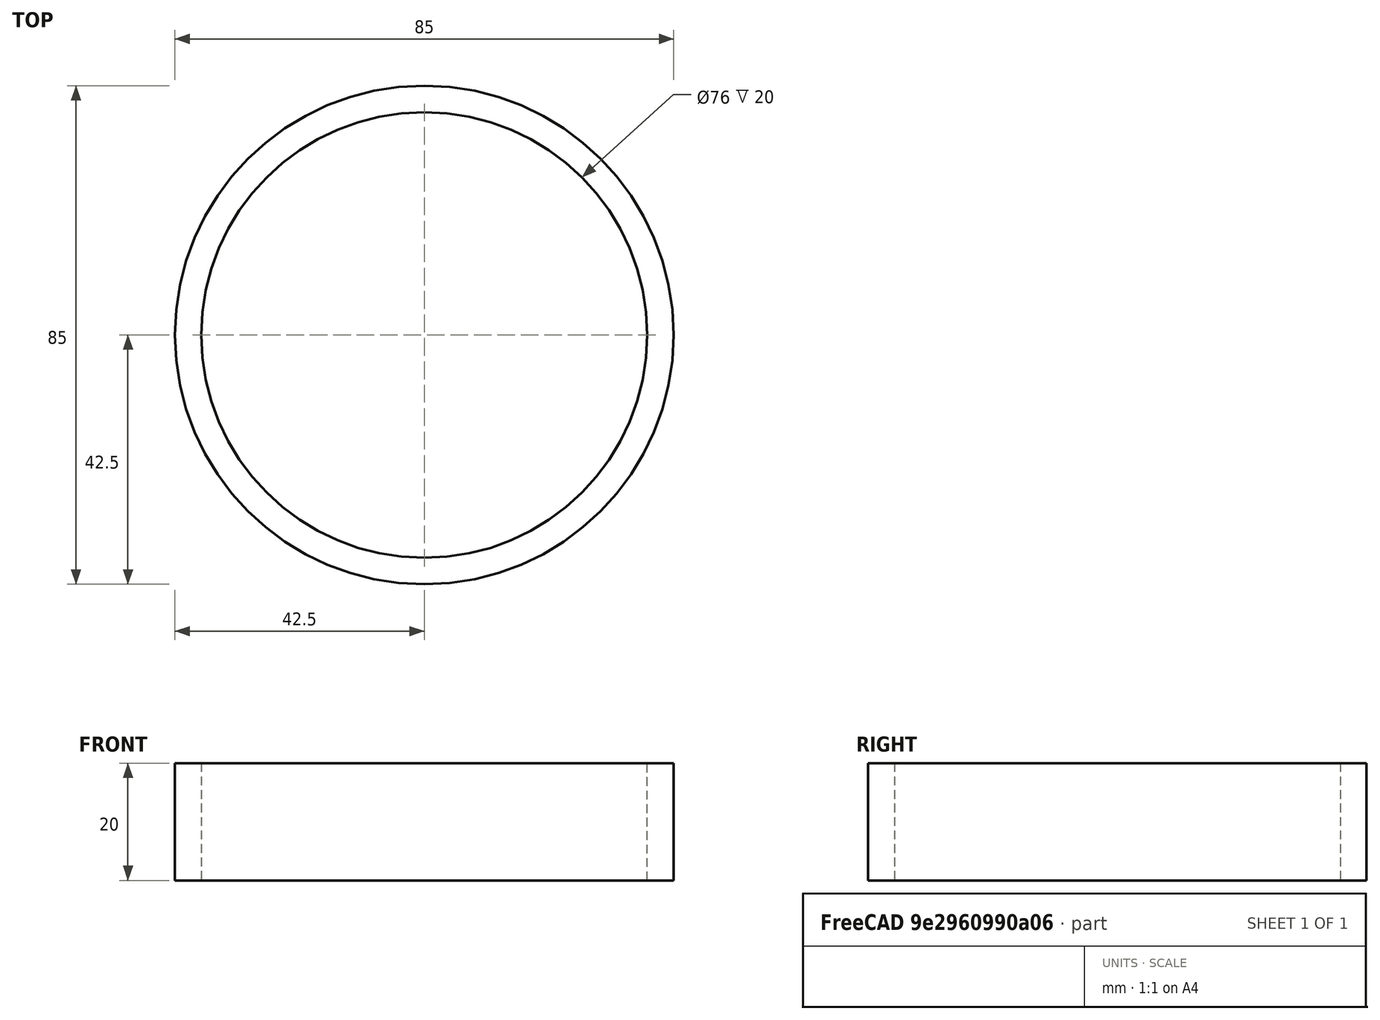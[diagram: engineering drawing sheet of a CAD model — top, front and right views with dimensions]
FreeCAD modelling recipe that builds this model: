
FCSTD DOCUMENT  (FreeCAD 0.19R24276 (Git))
Label: Ring_in_coil
License: All rights reserved
LicenseURL: http://en.wikipedia.org/wiki/All_rights_reserved
objects: Sketcher::SketchObject×1, PartDesign::Pad×1, PartDesign::Body×1
note: 4 computed .brp shape members not serialized (recipe doc carries the construction recipe); baked Part::Feature solids carry a one-line shape summary decoded from their .brp

FEATURE [Sketcher::SketchObject] Sketch
  FullyConstrained = true
  MapMode = 5
  Support = -> [XY_Plane]
  sketch-geometry (2):
    g0: Circle CenterX=0 CenterY=0 CenterZ=0 NormalX=0 NormalY=0 NormalZ=1 AngleXU=0 Radius=38
    g1: Circle CenterX=0 CenterY=0 CenterZ=0 NormalX=0 NormalY=0 NormalZ=1 AngleXU=0 Radius=42.5
  constraints (4):
    c: Coincident(g0,g-1)
    c: Coincident(g1,g0)
    c: Diameter(g0) = 76
    c: Diameter(g1) = 85
FEATURE [PartDesign::Pad] Pad
  Direction = (1,1,1)
  Length = 20
  Length2 = 100
  Profile = -> Sketch
  Type = 0
FEATURE [PartDesign::Body] Body
  Group = -> [Sketch,Pad]
  Origin = -> Origin
  Tip = -> Pad
